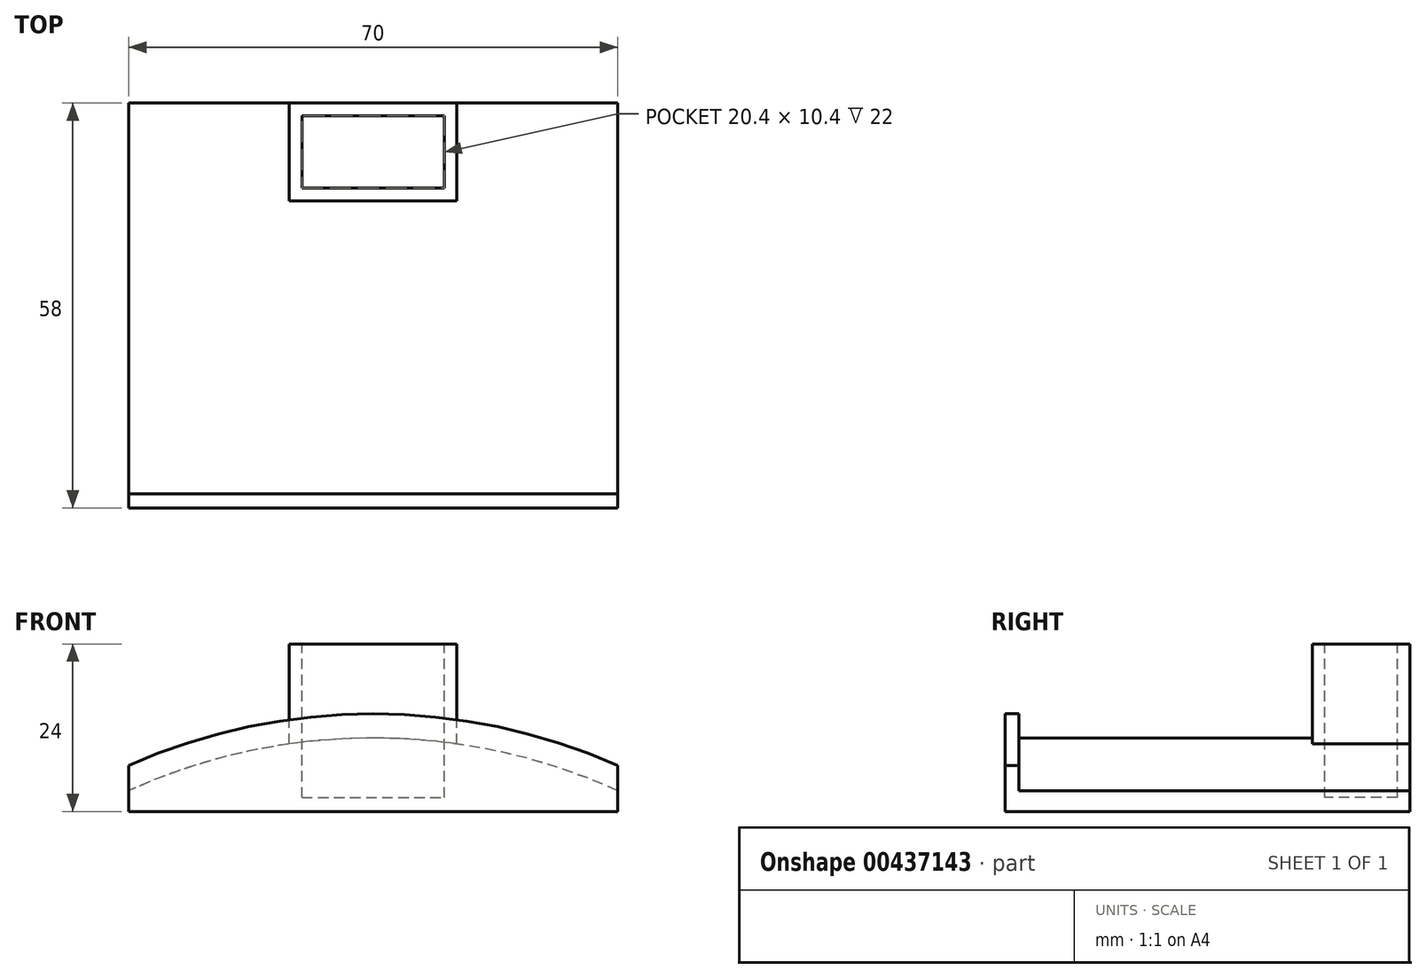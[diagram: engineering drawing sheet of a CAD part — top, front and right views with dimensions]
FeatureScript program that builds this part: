
annotation { "Feature Type Name" : "Feature", "Feature Type Description" : "" }
export const myFeature = defineFeature(function(context is Context, id is Id, definition is map)
    precondition{}
    {
        {
            var Q0;
            Q0=qCreatedBy(makeId("Front.planeOp"),FACE);
            var sketch = newSketch(context, id + "F0", { "sketchPlane" : qUnion([Q0])});
            skCircle(sketch, "E0", {"center": v(0, -77.46) * mm, "radius": 85 * mm});
            skLineSegment(sketch, "E1", {"start": v(-35, 0) * mm, "end": v(35, 0) * mm, "construction": true});
            skLineSegment(sketch, "E2.top", {"start": v(-35, -3) * mm, "end": v(35, -3) * mm});
            skLineSegment(sketch, "E2.left", {"start": v(-35, 0) * mm, "end": v(-35, -3) * mm});
            skLineSegment(sketch, "E2.right", {"start": v(35, 0) * mm, "end": v(35, -3) * mm});
            skLineSegment(sketch, "E3.bottom", {"start": v(12, 0) * mm, "end": v(-12, 0) * mm});
            skLineSegment(sketch, "E3.top", {"start": v(12, 21) * mm, "end": v(-12, 21) * mm});
            skLineSegment(sketch, "E3.left", {"start": v(12, 0) * mm, "end": v(12, 21) * mm});
            skLineSegment(sketch, "E3.right", {"start": v(-12, 0) * mm, "end": v(-12, 21) * mm});
            skLineSegment(sketch, "E4", {"start": v(0, 21) * mm, "end": v(0, 0) * mm, "construction": true});
            skSolve(sketch);
        }
        {
            var Q0;
            Q0=makeQuery(id+"F0.imprint","IMPRINT",FACE,{"disambiguationData":[TD([[makeQuery(id+"F0.imprint","IMPRINT",EDGE,{"derivedFrom":sQuery(id+"F0.wireOp",EDGE,"E2.top")}),1.0]])]});
            var Q1;
            {var subQ0=sQuery(id+"F0.wireOp",EDGE,"E3.right");var subQ1=sQuery(id+"F0.wireOp",EDGE,"E0");var subQ2=makeQuery(id+"F0.imprint","INTERSECT",VERTEX,{"derivedFrom":[subQ1,subQ0]});Q1=makeQuery(id+"F0.imprint","IMPRINT",FACE,{"disambiguationData":[TD([[makeQuery(id+"F0.imprint","IMPRINT",EDGE,{"disambiguationData":[TD([[subQ2,1.0]])],"derivedFrom":subQ1}),1.0]])]});}
            var Q2;
            {var subQ0=sQuery(id+"F0.wireOp",EDGE,"E3.left");var subQ1=sQuery(id+"F0.wireOp",EDGE,"E0");var subQ2=makeQuery(id+"F0.imprint","INTERSECT",VERTEX,{"derivedFrom":[subQ1,subQ0]});Q2=makeQuery(id+"F0.imprint","IMPRINT",FACE,{"disambiguationData":[TD([[makeQuery(id+"F0.imprint","IMPRINT",EDGE,{"disambiguationData":[TD([[subQ2,-1.0]])],"derivedFrom":subQ1}),1.0]])]});}
            extrude(context, id + "F1", {"entities" : qUnion([Q0, Q1, Q2]), "depth" : (42 + 16) * mm});
        }
        {
            var Q0;
            {var subQ5=sQuery(id+"F0.wireOp",EDGE,"E3.top");Q0=makeQuery(id+"F0.imprint","IMPRINT",FACE,{"disambiguationData":[TD([[makeQuery(id+"F0.imprint","IMPRINT",EDGE,{"derivedFrom":subQ5}),1.0]])]});}
            extrude(context, id + "F2", {"entities" : qUnion([Q0]), "operationType" : NewBodyOperationType.ADD, "depth" : 14 * mm});
        }
        {
            var Q0;
            Q0=makeQuery(id+"F1.opExtrude","CAP_FACE",FACE,{"disambiguationData":[OSD([sQuery(id+"F0.wireOp",EDGE,"E0"),sQuery(id+"F0.wireOp",EDGE,"E2.top"),sQuery(id+"F0.wireOp",EDGE,"E2.left"),sQuery(id+"F0.wireOp",EDGE,"E2.right")])],"isStart":false});
            var sketch = newSketch(context, id + "F3", { "sketchPlane" : qUnion([Q0])});
            skCircle(sketch, "E5", {"center": v(0, -75.5) * mm, "radius": 86.5 * mm});
            skLineSegment(sketch, "E6", {"start": v(0, 0) * mm, "end": v(0, -75.5) * mm});
            skLineSegment(sketch, "E7", {"start": v(-35, 0) * mm, "end": v(-35, 3.6) * mm});
            skLineSegment(sketch, "E8", {"start": v(35, 0) * mm, "end": v(35, 3.6) * mm});
            skSolve(sketch);
        }
        {
            var Q0;
            {var subQ0=sQuery(id+"F3.wireOp",EDGE,"E7");Q0=makeQuery(id+"F3.imprint","IMPRINT",FACE,{"disambiguationData":[TD([[makeQuery(id+"F3.imprint","IMPRINT",EDGE,{"derivedFrom":subQ0}),-1.0]])]});}
            extrude(context, id + "F4", {"entities" : qUnion([Q0]), "operationType" : NewBodyOperationType.ADD, "oppositeDirection" : true, "depth" : 2 * mm});
        }
        {
            var Q0;
            Q0=makeQuery(id+"F2.opExtrude","SWEPT_FACE",FACE,{"disambiguationData":[OSD([sQuery(id+"F0.wireOp",EDGE,"E3.top")])]});
            var sketch = newSketch(context, id + "F5", { "sketchPlane" : qUnion([Q0])});
            skLineSegment(sketch, "E9.bottom", {"start": v(-10.2, -1.8) * mm, "end": v(10.2, -1.8) * mm});
            skLineSegment(sketch, "E9.top", {"start": v(-10.2, -12.2) * mm, "end": v(10.2, -12.2) * mm});
            skLineSegment(sketch, "E9.left", {"start": v(-10.2, -1.8) * mm, "end": v(-10.2, -12.2) * mm});
            skLineSegment(sketch, "E9.right", {"start": v(10.2, -1.8) * mm, "end": v(10.2, -12.2) * mm});
            skSolve(sketch);
        }
        {
            var Q0;
            Q0=makeQuery(id+"F5.imprint","IMPRINT",FACE,{"disambiguationData":[TD([[makeQuery(id+"F5.imprint","IMPRINT",EDGE,{"derivedFrom":sQuery(id+"F5.wireOp",EDGE,"E9.bottom")}),-1.0]])]});
            extrude(context, id + "F6", {"entities" : qUnion([Q0]), "operationType" : NewBodyOperationType.REMOVE, "oppositeDirection" : true, "depth" : 22 * mm});
        }
    });
